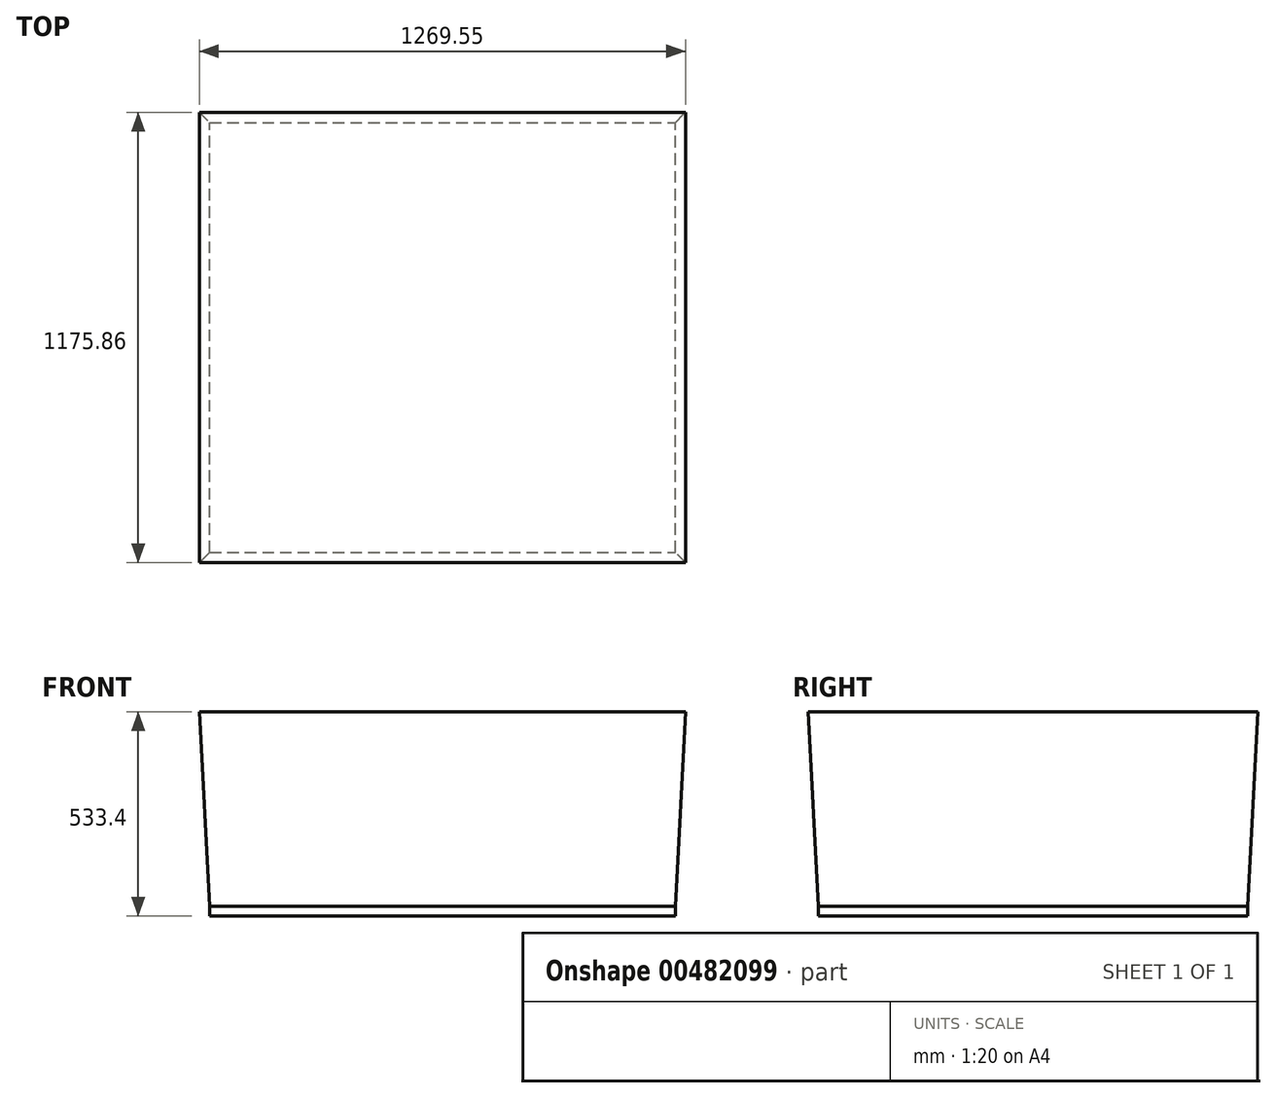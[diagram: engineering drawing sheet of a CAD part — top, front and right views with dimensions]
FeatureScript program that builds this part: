
annotation { "Feature Type Name" : "Feature", "Feature Type Description" : "" }
export const myFeature = defineFeature(function(context is Context, id is Id, definition is map)
    precondition{}
    {
        {
            var Q0;
            Q0=qCreatedBy(makeId("Top.planeOp"),FACE);
            var sketch = newSketch(context, id + "F0", { "sketchPlane" : qUnion([Q0])});
            skLineSegment(sketch, "E0.bottom", {"start": v(-109.52, -186.74) * mm, "end": v(1106.79, -186.74) * mm});
            skLineSegment(sketch, "E0.top", {"start": v(-109.52, 935.87) * mm, "end": v(1106.79, 935.87) * mm});
            skLineSegment(sketch, "E0.left", {"start": v(-109.52, -186.74) * mm, "end": v(-109.52, 935.87) * mm});
            skLineSegment(sketch, "E0.right", {"start": v(1106.79, -186.74) * mm, "end": v(1106.79, 935.87) * mm});
            skSolve(sketch);
        }
        {
            var Q0;
            Q0=makeQuery(id+"F0.imprint","IMPRINT",FACE,{"disambiguationData":[TD([[makeQuery(id+"F0.imprint","IMPRINT",EDGE,{"derivedFrom":sQuery(id+"F0.wireOp",EDGE,"E0.bottom")}),1.0]])]});
            extrude(context, id + "F1", {"entities" : qUnion([Q0]), "depth" : 508 * mm, "hasDraft" : true, "draftAngle" : 3 * degree, "hasSecondDirection" : true, "secondDirectionOppositeDirection" : true, "secondDirectionDepth" : 25.4 * mm});
        }
    });
